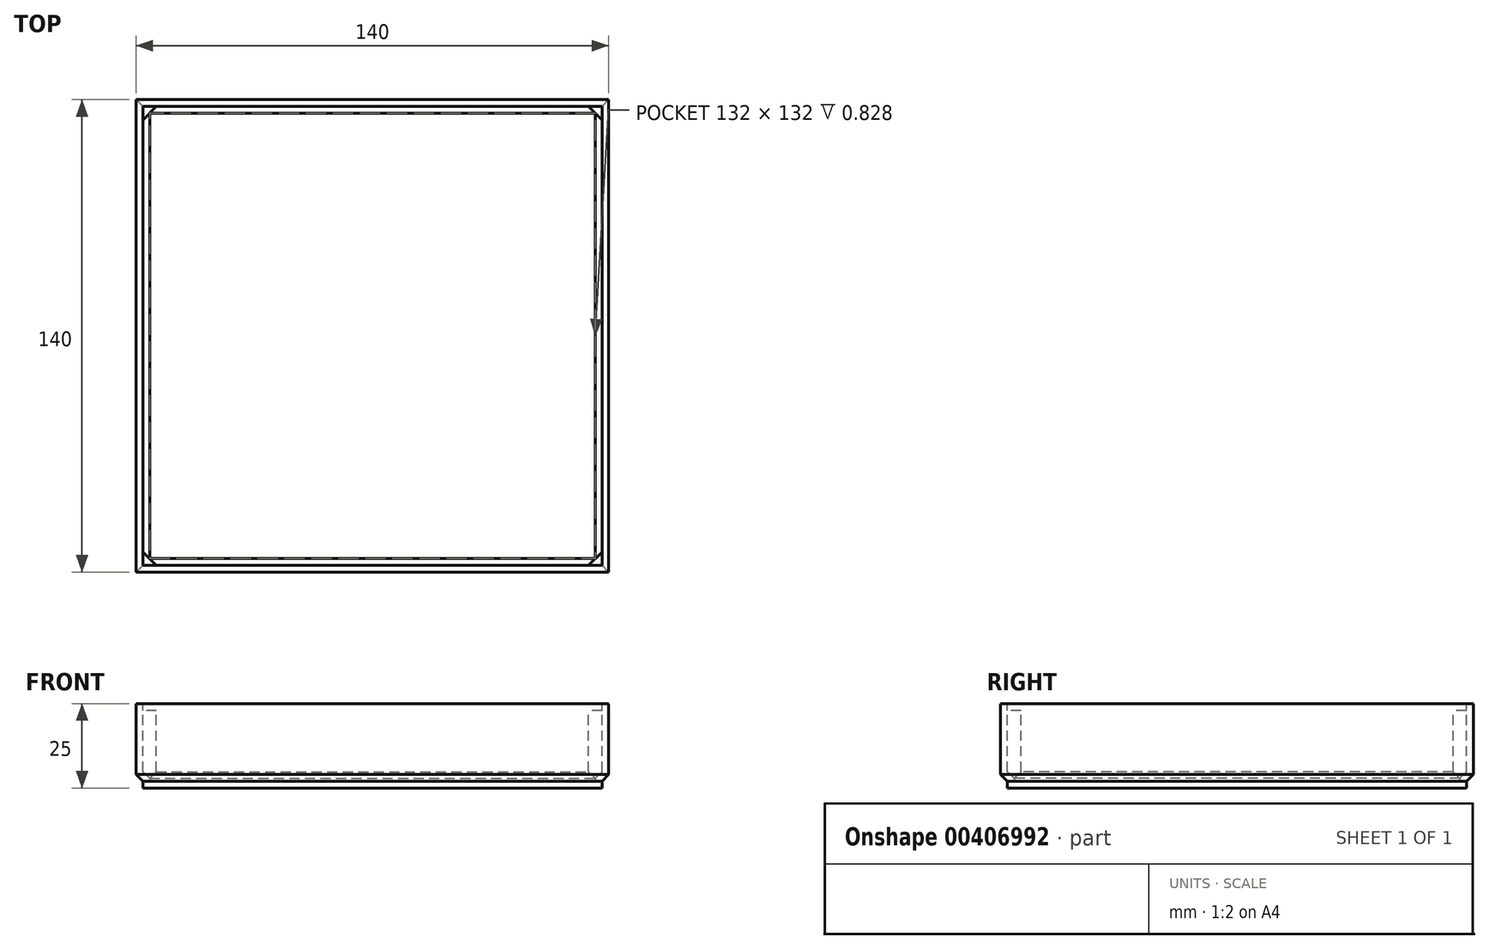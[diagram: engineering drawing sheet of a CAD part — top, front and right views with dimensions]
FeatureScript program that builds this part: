
annotation { "Feature Type Name" : "Feature", "Feature Type Description" : "" }
export const myFeature = defineFeature(function(context is Context, id is Id, definition is map)
    precondition{}
    {
        {
            var Q0;
            Q0=qCreatedBy(makeId("Front.planeOp"),FACE);
            var sketch = newSketch(context, id + "F0", { "sketchPlane" : qUnion([Q0])});
            skLineSegment(sketch, "E0.bottom", {"start": v(0, 0) * mm, "end": v(68, 0) * mm});
            skLineSegment(sketch, "E0.top", {"start": v(0, 25) * mm, "end": v(70, 25) * mm});
            skLineSegment(sketch, "E0.left", {"start": v(0, 0) * mm, "end": v(0, 25) * mm});
            skLineSegment(sketch, "E0.right", {"start": v(70, 4) * mm, "end": v(70, 25) * mm});
            skLineSegment(sketch, "E1", {"start": v(68, 2) * mm, "end": v(68, 2) * mm});
            skLineSegment(sketch, "E2", {"start": v(68, 2) * mm, "end": v(68, 0) * mm});
            skPoint(sketch, "E3.orphan", {"position": v(70, 0) * mm});
            skPoint(sketch, "E4.visualSharp", {"position": v(70, 2) * mm});
            skLineSegment(sketch, "E5", {"start": v(70, 4) * mm, "end": v(68, 2) * mm});
            skSolve(sketch);
        }
        {
            var Q0;
            Q0=makeQuery(id+"F0.imprint","IMPRINT",FACE,{"disambiguationData":[TD([[makeQuery(id+"F0.imprint","IMPRINT",EDGE,{"derivedFrom":sQuery(id+"F0.wireOp",EDGE,"E0.bottom")}),1.0]])]});
            extrude(context, id + "F1", {"entities" : qUnion([Q0]), "oppositeDirection" : true, "depth" : 70 * mm});
        }
        {
            var Q0;
            Q0=qCreatedBy(makeId("Right.planeOp"),FACE);
            var sketch = newSketch(context, id + "F2", { "sketchPlane" : qUnion([Q0])});
            skLineSegment(sketch, "E6.bottom", {"start": v(0, 0) * mm, "end": v(68, 0) * mm});
            skLineSegment(sketch, "E6.top", {"start": v(0, 25) * mm, "end": v(70, 25) * mm});
            skLineSegment(sketch, "E6.left", {"start": v(0, 0) * mm, "end": v(0, 25) * mm});
            skLineSegment(sketch, "E6.right", {"start": v(70, 4) * mm, "end": v(70, 25) * mm});
            skLineSegment(sketch, "E7", {"start": v(68, 2) * mm, "end": v(68, 2) * mm});
            skLineSegment(sketch, "E8", {"start": v(68, 2) * mm, "end": v(68, 0) * mm});
            skPoint(sketch, "E9.orphan", {"position": v(70, 0) * mm});
            skPoint(sketch, "E10.visualSharp", {"position": v(70, 2) * mm});
            skLineSegment(sketch, "E11", {"start": v(68, 2) * mm, "end": v(70, 4) * mm});
            skSolve(sketch);
        }
        {
            var Q0;
            Q0 = qSketchRegion(id + "F2", true);
            var Q1;
            Q1=makeQuery(id+"F1.opExtrude","SWEPT_FACE",FACE,{"disambiguationData":[OSD([sQuery(id+"F0.wireOp",EDGE,"E0.right")])]});
            extrude(context, id + "F3", {"entities" : qUnion([Q0]), "operationType" : NewBodyOperationType.INTERSECT, "endBound" : BoundingType.UP_TO_SURFACE, "endBoundEntityFace" : qUnion([Q1]), "depth" : 25 * mm});
        }
        {
            var Q0;
            Q0=makeQuery(id+"F1.opExtrude","SWEPT_BODY",BODY,{"disambiguationData":[OSD([sQuery(id+"F0.wireOp",EDGE,"E0.bottom"),sQuery(id+"F0.wireOp",EDGE,"E0.top"),sQuery(id+"F0.wireOp",EDGE,"E0.left"),sQuery(id+"F0.wireOp",EDGE,"E0.right"),sQuery(id+"F0.wireOp",EDGE,"E2"),sQuery(id+"F0.wireOp",EDGE,"E4.filletArc")])]});
            var Q1;
            Q1=makeQuery(id+"F1.opExtrude","CAP_EDGE",EDGE,{"disambiguationData":[OSD([sQuery(id+"F0.wireOp",EDGE,"E0.left")])],"isStart":true});
            circularPattern(context, id + "F4", {"operationType" : NewBodyOperationType.ADD, "entities" : qUnion([Q0]), "axis" : qUnion([Q1]), "angle" : 360 * degree, "instanceCount" : 4, "equalSpace" : true});
        }
        {
            var Q0;
            {var subQ0=makeQuery(id+"F1.opExtrude","SWEPT_FACE",FACE,{"disambiguationData":[OSD([sQuery(id+"F0.wireOp",EDGE,"E0.top")])]});Q0=makeQuery(id+"F4.boolean.opBoolean","MERGE",FACE,{"derivedFrom":[subQ0,makeQuery(id+"F4.opPattern","COPY",FACE,{"derivedFrom":subQ0,"instanceName":"1"}),makeQuery(id+"F4.opPattern","COPY",FACE,{"derivedFrom":subQ0,"instanceName":"2"}),makeQuery(id+"F4.opPattern","COPY",FACE,{"derivedFrom":subQ0,"instanceName":"3"})]});}
            shell(context, id + "F5", {"entities" : qUnion([Q0]), "thickness" : 2 * mm});
        }
        {
            var Q0;
            {var subQ0=makeQuery(id+"F1.opExtrude","SWEPT_FACE",FACE,{"disambiguationData":[OSD([sQuery(id+"F0.wireOp",EDGE,"E0.top")])]});Q0=makeQuery(id+"F4.boolean.opBoolean","MERGE",FACE,{"derivedFrom":[subQ0,makeQuery(id+"F4.opPattern","COPY",FACE,{"derivedFrom":subQ0,"instanceName":"1"}),makeQuery(id+"F4.opPattern","COPY",FACE,{"derivedFrom":subQ0,"instanceName":"2"}),makeQuery(id+"F4.opPattern","COPY",FACE,{"derivedFrom":subQ0,"instanceName":"3"})]});}
            var sketch = newSketch(context, id + "F6", { "sketchPlane" : qUnion([Q0])});
            skLineSegment(sketch, "E12.0", {"start": v(-68, 68) * mm, "end": v(68, 68) * mm});
            skLineSegment(sketch, "E13.0", {"start": v(-68, -68) * mm, "end": v(-68, 68) * mm});
            skLineSegment(sketch, "E14.0", {"start": v(66, 66) * mm, "end": v(-66, 66) * mm});
            skLineSegment(sketch, "E15.0", {"start": v(-66, 66) * mm, "end": v(-66, -66) * mm});
            skLineSegment(sketch, "E16", {"start": v(-64, 68) * mm, "end": v(-68, 64) * mm});
            skLineSegment(sketch, "E17", {"start": v(0, 82.2) * mm, "end": v(0, -88.58) * mm, "construction": true});
            skPoint(sketch, "E17.startSnap0", {"position": v(0, 70) * mm});
            skPoint(sketch, "E17.endSnap0", {"position": v(0, -70) * mm});
            skLineSegment(sketch, "E18", {"start": v(-101.44, 0) * mm, "end": v(107.4, 0) * mm, "construction": true});
            skPoint(sketch, "E18.startSnap0", {"position": v(-70, 0) * mm});
            skLineSegment(sketch, "E19.MirrorCS", {"start": v(64, 68) * mm, "end": v(68, 64) * mm});
            skLineSegment(sketch, "E20.MirrorCS", {"start": v(64, -68) * mm, "end": v(68, -64) * mm});
            skLineSegment(sketch, "E21.MirrorCS", {"start": v(-64, -68) * mm, "end": v(-68, -64) * mm});
            skSolve(sketch);
        }
        {
            var Q0;
            {var subQ5=sQuery(id+"F6.wireOp",EDGE,"E21.MirrorCS");var subQ7=makeQuery(id+"F6.imprint","INTERSECT",VERTEX,{"derivedFrom":[sQuery(id+"F6.wireOp",EDGE,"E15.0"),subQ5]});Q0=makeQuery(id+"F6.imprint","IMPRINT",FACE,{"disambiguationData":[TD([[makeQuery(id+"F6.imprint","IMPRINT",EDGE,{"disambiguationData":[TD([[subQ7,-1.0]])],"derivedFrom":subQ5}),1.0]])]});}
            var Q1;
            {var subQ0=sQuery(id+"F6.wireOp",EDGE,"E20.MirrorCS");Q1=makeQuery(id+"F6.imprint","IMPRINT",FACE,{"disambiguationData":[TD([[makeQuery(id+"F6.imprint","IMPRINT",EDGE,{"derivedFrom":subQ0}),-1.0]])]});}
            var Q2;
            {var subQ5=sQuery(id+"F6.wireOp",EDGE,"E19.MirrorCS");var subQ7=makeQuery(id+"F6.imprint","INTERSECT",VERTEX,{"derivedFrom":[sQuery(id+"F6.wireOp",EDGE,"E14.0"),subQ5]});Q2=makeQuery(id+"F6.imprint","IMPRINT",FACE,{"disambiguationData":[TD([[makeQuery(id+"F6.imprint","IMPRINT",EDGE,{"disambiguationData":[TD([[subQ7,1.0]])],"derivedFrom":subQ5}),1.0]])]});}
            var Q3;
            {var subQ0=sQuery(id+"F6.wireOp",EDGE,"E13.0");var subQ1=sQuery(id+"F6.wireOp",EDGE,"E12.0");var subQ2=makeQuery(id+"F6.imprint","INTERSECT",VERTEX,{"derivedFrom":[subQ1,subQ0]});Q3=makeQuery(id+"F6.imprint","IMPRINT",FACE,{"disambiguationData":[TD([[makeQuery(id+"F6.imprint","IMPRINT",EDGE,{"disambiguationData":[TD([[subQ2,-1.0]])],"derivedFrom":subQ1}),-1.0]])]});}
            var Q4;
            Q4=makeQuery(id+"F5.opShell","OFFSET_FACE",FACE,{"disambiguationData":[OSD([sQuery(id+"F0.wireOp",EDGE,"E0.bottom")])]});
            extrude(context, id + "F7", {"entities" : qUnion([Q0, Q1, Q2, Q3]), "operationType" : NewBodyOperationType.ADD, "endBound" : BoundingType.UP_TO_SURFACE, "oppositeDirection" : true, "endBoundEntityFace" : qUnion([Q4]), "depth" : 25 * mm});
        }
        {
            var Q0;
            {var subQ0=sQuery(id+"F6.wireOp",EDGE,"E20.MirrorCS");Q0=makeQuery(id+"F6.imprint","IMPRINT",FACE,{"disambiguationData":[TD([[makeQuery(id+"F6.imprint","IMPRINT",EDGE,{"derivedFrom":subQ0}),-1.0]])]});}
            var Q1;
            {var subQ5=sQuery(id+"F6.wireOp",EDGE,"E19.MirrorCS");var subQ7=makeQuery(id+"F6.imprint","INTERSECT",VERTEX,{"derivedFrom":[sQuery(id+"F6.wireOp",EDGE,"E14.0"),subQ5]});Q1=makeQuery(id+"F6.imprint","IMPRINT",FACE,{"disambiguationData":[TD([[makeQuery(id+"F6.imprint","IMPRINT",EDGE,{"disambiguationData":[TD([[subQ7,1.0]])],"derivedFrom":subQ5}),1.0]])]});}
            var Q2;
            {var subQ0=sQuery(id+"F6.wireOp",EDGE,"E13.0");var subQ1=sQuery(id+"F6.wireOp",EDGE,"E12.0");var subQ2=makeQuery(id+"F6.imprint","INTERSECT",VERTEX,{"derivedFrom":[subQ1,subQ0]});Q2=makeQuery(id+"F6.imprint","IMPRINT",FACE,{"disambiguationData":[TD([[makeQuery(id+"F6.imprint","IMPRINT",EDGE,{"disambiguationData":[TD([[subQ2,-1.0]])],"derivedFrom":subQ1}),-1.0]])]});}
            var Q3;
            {var subQ5=sQuery(id+"F6.wireOp",EDGE,"E21.MirrorCS");var subQ7=makeQuery(id+"F6.imprint","INTERSECT",VERTEX,{"derivedFrom":[sQuery(id+"F6.wireOp",EDGE,"E15.0"),subQ5]});Q3=makeQuery(id+"F6.imprint","IMPRINT",FACE,{"disambiguationData":[TD([[makeQuery(id+"F6.imprint","IMPRINT",EDGE,{"disambiguationData":[TD([[subQ7,-1.0]])],"derivedFrom":subQ5}),1.0]])]});}
            extrude(context, id + "F8", {"entities" : qUnion([Q0, Q1, Q2, Q3]), "operationType" : NewBodyOperationType.REMOVE, "oppositeDirection" : true, "depth" : 2 * mm});
        }
    });
